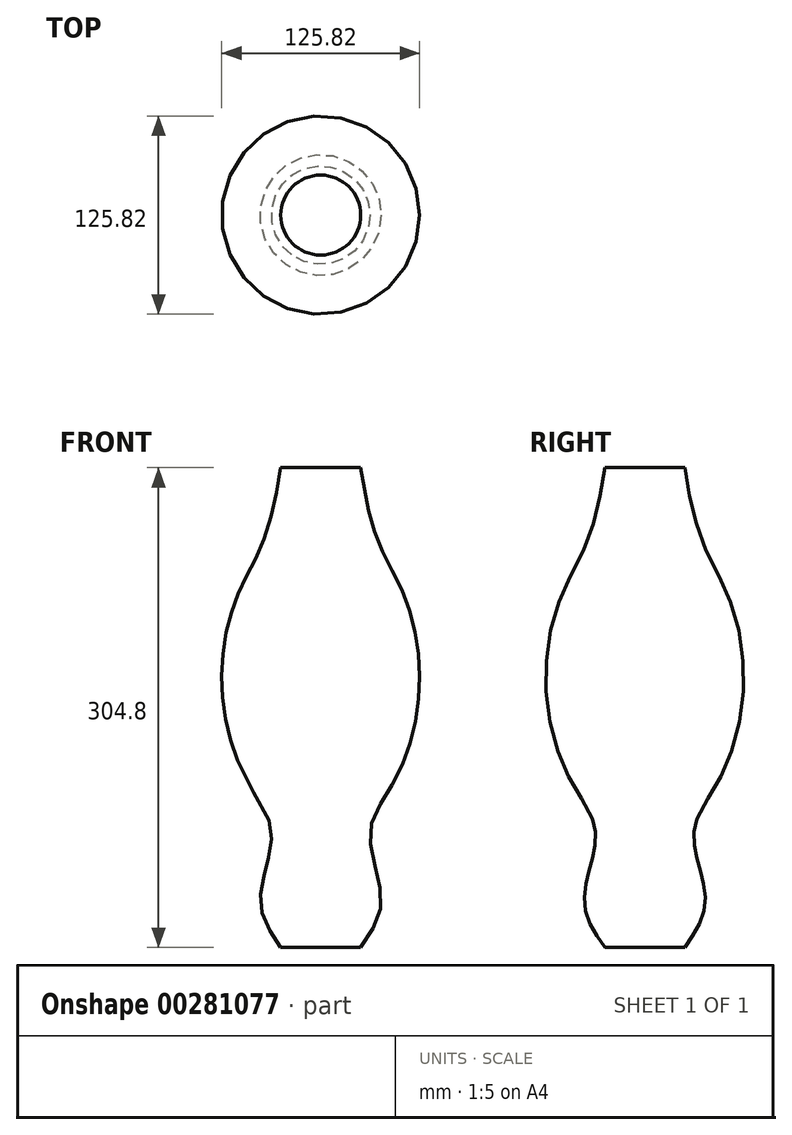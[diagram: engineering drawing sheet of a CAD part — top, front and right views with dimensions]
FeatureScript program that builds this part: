
annotation { "Feature Type Name" : "Feature", "Feature Type Description" : "" }
export const myFeature = defineFeature(function(context is Context, id is Id, definition is map)
    precondition{}
    {
        {
            var Q0;
            Q0=qCreatedBy(makeId("Top.planeOp"),FACE);
            cPlane(context, id + "F0", {"entities" : qUnion([Q0]), "cplaneType" : CPlaneType.OFFSET, "offset" : 25.4 * mm, "width" : 152.4 * mm, "height" : 152.4 * mm});
        }
        {
            var Q0;
            Q0=qCreatedBy(id+"F0.planeOp",FACE);
            cPlane(context, id + "F1", {"entities" : qUnion([Q0]), "cplaneType" : CPlaneType.OFFSET, "offset" : 50.8 * mm, "width" : 152.4 * mm, "height" : 152.4 * mm});
        }
        {
            var Q0;
            Q0=qCreatedBy(id+"F1.planeOp",FACE);
            cPlane(context, id + "F2", {"entities" : qUnion([Q0]), "cplaneType" : CPlaneType.OFFSET, "offset" : 25.4 * mm, "width" : 152.4 * mm, "height" : 152.4 * mm});
        }
        {
            var Q0;
            Q0=qCreatedBy(id+"F2.planeOp",FACE);
            cPlane(context, id + "F3", {"entities" : qUnion([Q0]), "cplaneType" : CPlaneType.OFFSET, "offset" : 127 * mm, "width" : 152.4 * mm, "height" : 152.4 * mm});
        }
        {
            var Q0;
            Q0=qCreatedBy(id+"F3.planeOp",FACE);
            cPlane(context, id + "F4", {"entities" : qUnion([Q0]), "cplaneType" : CPlaneType.OFFSET, "offset" : 25.4 * mm, "width" : 152.4 * mm, "height" : 152.4 * mm});
        }
        {
            var Q0;
            Q0=qCreatedBy(id+"F4.planeOp",FACE);
            cPlane(context, id + "F5", {"entities" : qUnion([Q0]), "cplaneType" : CPlaneType.OFFSET, "offset" : 50.8 * mm, "width" : 152.4 * mm, "height" : 152.4 * mm});
        }
        {
            var Q0;
            Q0=qCreatedBy(makeId("Top.planeOp"),FACE);
            var sketch = newSketch(context, id + "F6", { "sketchPlane" : qUnion([Q0])});
            skCircle(sketch, "E0", {"center": v(0, 0) * mm, "radius": 25.4 * mm});
            skSolve(sketch);
        }
        {
            var Q0;
            Q0=qCreatedBy(id+"F0.planeOp",FACE);
            var sketch = newSketch(context, id + "F7", { "sketchPlane" : qUnion([Q0])});
            skCircle(sketch, "E1", {"center": v(0, 0) * mm, "radius": 38.1 * mm});
            skSolve(sketch);
        }
        {
            var Q0;
            Q0=qCreatedBy(id+"F1.planeOp",FACE);
            var sketch = newSketch(context, id + "F8", { "sketchPlane" : qUnion([Q0])});
            skCircle(sketch, "E2", {"center": v(0, 0) * mm, "radius": 31.75 * mm});
            skSolve(sketch);
        }
        {
            var Q0;
            Q0=qCreatedBy(id+"F2.planeOp",FACE);
            var sketch = newSketch(context, id + "F9", { "sketchPlane" : qUnion([Q0])});
            skCircle(sketch, "E3", {"center": v(0, 0) * mm, "radius": 44.45 * mm});
            skSolve(sketch);
        }
        {
            var Q0;
            Q0=qCreatedBy(id+"F3.planeOp",FACE);
            var sketch = newSketch(context, id + "F10", { "sketchPlane" : qUnion([Q0])});
            skCircle(sketch, "E4", {"center": v(0, 0) * mm, "radius": 50.8 * mm});
            skSolve(sketch);
        }
        {
            var Q0;
            Q0=qCreatedBy(id+"F4.planeOp",FACE);
            var sketch = newSketch(context, id + "F11", { "sketchPlane" : qUnion([Q0])});
            skCircle(sketch, "E5", {"center": v(0, 0) * mm, "radius": 38.1 * mm});
            skSolve(sketch);
        }
        {
            var Q0;
            Q0=qCreatedBy(id+"F5.planeOp",FACE);
            var sketch = newSketch(context, id + "F12", { "sketchPlane" : qUnion([Q0])});
            skCircle(sketch, "E6", {"center": v(0, 0) * mm, "radius": 25.4 * mm});
            skSolve(sketch);
        }
        {
            var Q0;
            Q0=makeQuery(id+"F12.imprint","IMPRINT",FACE,{"disambiguationData":[TD([[makeQuery(id+"F12.imprint","IMPRINT",EDGE,{"derivedFrom":sQuery(id+"F12.wireOp",EDGE,"E6")}),1.0]])]});
            var Q1;
            Q1=makeQuery(id+"F11.imprint","IMPRINT",FACE,{"disambiguationData":[TD([[makeQuery(id+"F11.imprint","IMPRINT",EDGE,{"derivedFrom":sQuery(id+"F11.wireOp",EDGE,"E5")}),1.0]])]});
            var Q2;
            Q2=makeQuery(id+"F10.imprint","IMPRINT",FACE,{"disambiguationData":[TD([[makeQuery(id+"F10.imprint","IMPRINT",EDGE,{"derivedFrom":sQuery(id+"F10.wireOp",EDGE,"E4")}),1.0]])]});
            var Q3;
            Q3=makeQuery(id+"F9.imprint","IMPRINT",FACE,{"disambiguationData":[TD([[makeQuery(id+"F9.imprint","IMPRINT",EDGE,{"derivedFrom":sQuery(id+"F9.wireOp",EDGE,"E3")}),1.0]])]});
            var Q4;
            Q4=makeQuery(id+"F8.imprint","IMPRINT",FACE,{"disambiguationData":[TD([[makeQuery(id+"F8.imprint","IMPRINT",EDGE,{"derivedFrom":sQuery(id+"F8.wireOp",EDGE,"E2")}),1.0]])]});
            var Q5;
            Q5=makeQuery(id+"F7.imprint","IMPRINT",FACE,{"disambiguationData":[TD([[makeQuery(id+"F7.imprint","IMPRINT",EDGE,{"derivedFrom":sQuery(id+"F7.wireOp",EDGE,"E1")}),1.0]])]});
            var Q6;
            Q6=makeQuery(id+"F6.imprint","IMPRINT",FACE,{"disambiguationData":[TD([[makeQuery(id+"F6.imprint","IMPRINT",EDGE,{"derivedFrom":sQuery(id+"F6.wireOp",EDGE,"E0")}),1.0]])]});
            loft(context, id + "F13", {"sheetProfilesArray" : [{ "sheetProfileEntities" : qUnion([Q0]) }, { "sheetProfileEntities" : qUnion([Q1]) }, { "sheetProfileEntities" : qUnion([Q2]) }, { "sheetProfileEntities" : qUnion([Q3]) }, { "sheetProfileEntities" : qUnion([Q4]) }, { "sheetProfileEntities" : qUnion([Q5]) }, { "sheetProfileEntities" : qUnion([Q6]) }]});
        }
    });
